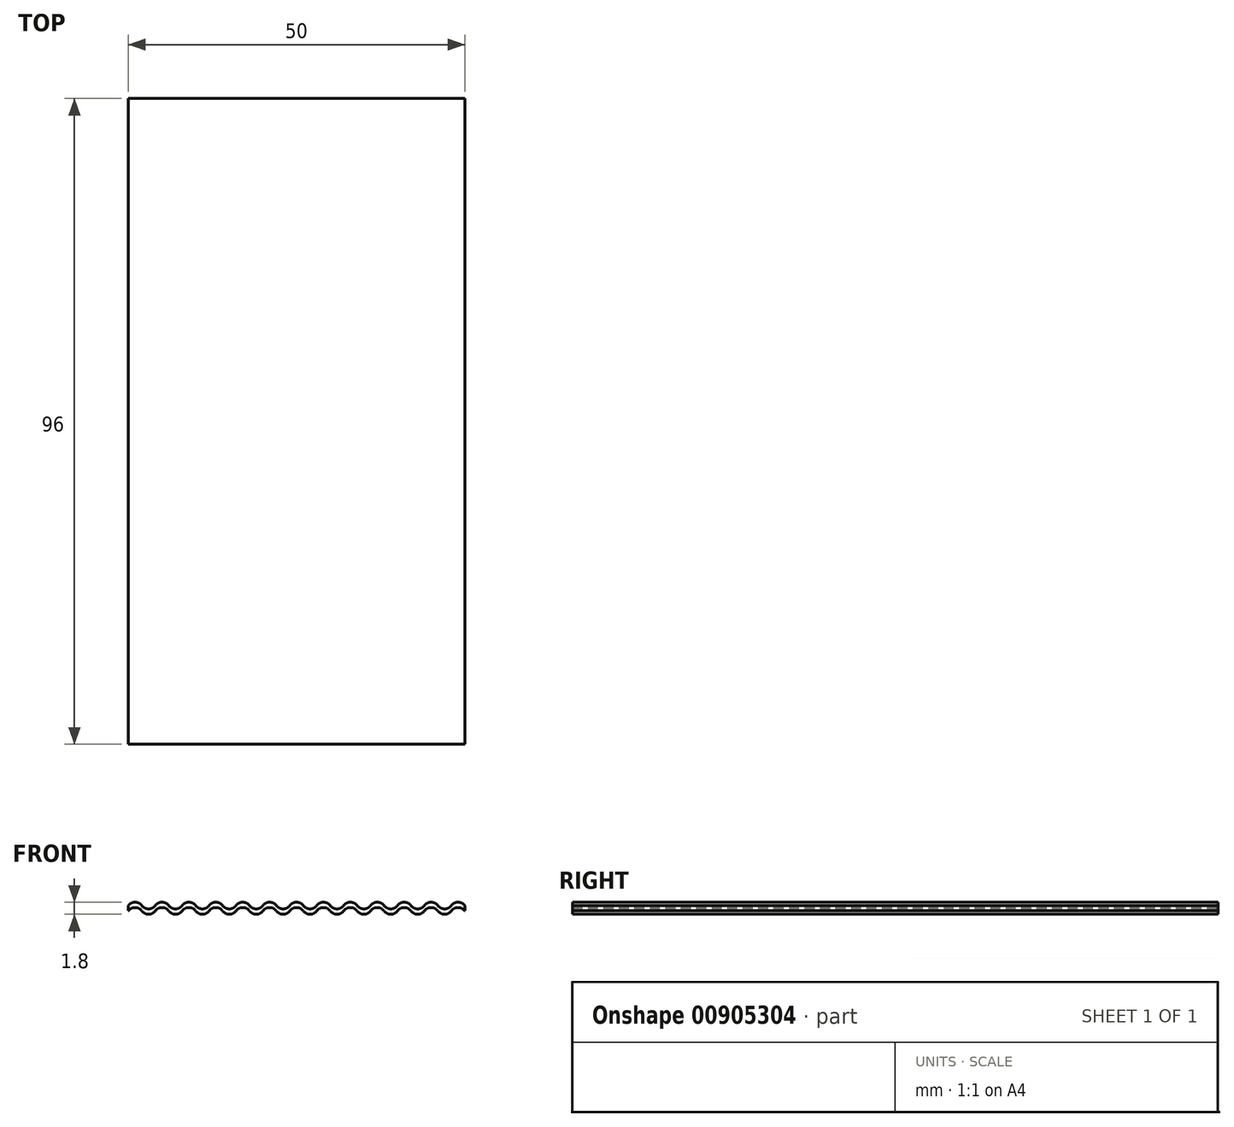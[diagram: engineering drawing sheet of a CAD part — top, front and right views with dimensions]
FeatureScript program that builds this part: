
annotation { "Feature Type Name" : "Feature", "Feature Type Description" : "" }
export const myFeature = defineFeature(function(context is Context, id is Id, definition is map)
    precondition{}
    {
        {
            var Q0;
            Q0=qCreatedBy(makeId("Front.planeOp"),FACE);
            var sketch = newSketch(context, id + "F0", { "sketchPlane" : qUnion([Q0])});
            skArc(sketch, "E0", {"start": v(-19, -0.4) * mm, "mid": v(-20, 0.1) * mm, "end": v(-21, -0.4) * mm});
            skArc(sketch, "E1", {"start": v(-23, -0.4) * mm, "mid": v(-22, -0.9) * mm, "end": v(-21, -0.4) * mm});
            skArc(sketch, "E2", {"start": v(-23, -0.4) * mm, "mid": v(-24, 0.1) * mm, "end": v(-25, -0.4) * mm});
            skArc(sketch, "E3", {"start": v(5, -0.4) * mm, "mid": v(6, -0.9) * mm, "end": v(7, -0.4) * mm});
            skArc(sketch, "E4", {"start": v(9, -0.4) * mm, "mid": v(8, 0.1) * mm, "end": v(7, -0.4) * mm});
            skArc(sketch, "E5", {"start": v(9, -0.4) * mm, "mid": v(10, -0.9) * mm, "end": v(11, -0.4) * mm});
            skArc(sketch, "E6", {"start": v(13, -0.4) * mm, "mid": v(12, 0.1) * mm, "end": v(11, -0.4) * mm});
            skArc(sketch, "E7", {"start": v(13, -0.4) * mm, "mid": v(14, -0.9) * mm, "end": v(15, -0.4) * mm});
            skArc(sketch, "E8", {"start": v(17, -0.4) * mm, "mid": v(16, 0.1) * mm, "end": v(15, -0.4) * mm});
            skArc(sketch, "E9", {"start": v(25, -0.4) * mm, "mid": v(24, 0.1) * mm, "end": v(23, -0.4) * mm});
            skArc(sketch, "E10", {"start": v(21, -0.4) * mm, "mid": v(22, -0.9) * mm, "end": v(23, -0.4) * mm});
            skArc(sketch, "E11", {"start": v(21, -0.4) * mm, "mid": v(20, 0.1) * mm, "end": v(19, -0.4) * mm});
            skArc(sketch, "E12", {"start": v(17, -0.4) * mm, "mid": v(18, -0.9) * mm, "end": v(19, -0.4) * mm});
            skArc(sketch, "E13", {"start": v(5, -0.4) * mm, "mid": v(4, 0.1) * mm, "end": v(3, -0.4) * mm});
            skArc(sketch, "E14", {"start": v(1, -0.4) * mm, "mid": v(2, -0.9) * mm, "end": v(3, -0.4) * mm});
            skArc(sketch, "E15", {"start": v(1, -0.4) * mm, "mid": v(0, 0.1) * mm, "end": v(-1, -0.4) * mm});
            skArc(sketch, "E16", {"start": v(-3, -0.4) * mm, "mid": v(-2, -0.9) * mm, "end": v(-1, -0.4) * mm});
            skArc(sketch, "E17", {"start": v(-3, -0.4) * mm, "mid": v(-4, 0.1) * mm, "end": v(-5, -0.4) * mm});
            skArc(sketch, "E18", {"start": v(-7, -0.4) * mm, "mid": v(-6, -0.9) * mm, "end": v(-5, -0.4) * mm});
            skArc(sketch, "E19", {"start": v(-7, -0.4) * mm, "mid": v(-8, 0.1) * mm, "end": v(-9, -0.4) * mm});
            skArc(sketch, "E20", {"start": v(-11, -0.4) * mm, "mid": v(-10, -0.9) * mm, "end": v(-9, -0.4) * mm});
            skArc(sketch, "E21", {"start": v(-11, -0.4) * mm, "mid": v(-12, 0.1) * mm, "end": v(-13, -0.4) * mm});
            skArc(sketch, "E22", {"start": v(-15, -0.4) * mm, "mid": v(-14, -0.9) * mm, "end": v(-13, -0.4) * mm});
            skArc(sketch, "E23", {"start": v(-15, -0.4) * mm, "mid": v(-16, 0.1) * mm, "end": v(-17, -0.4) * mm});
            skArc(sketch, "E24", {"start": v(-19, -0.4) * mm, "mid": v(-18, -0.9) * mm, "end": v(-17, -0.4) * mm});
            skArc(sketch, "E25", {"start": v(-19, 0.4) * mm, "mid": v(-20, 0.9) * mm, "end": v(-21, 0.4) * mm});
            skArc(sketch, "E26", {"start": v(-23, 0.4) * mm, "mid": v(-22, -0.1) * mm, "end": v(-21, 0.4) * mm});
            skArc(sketch, "E27", {"start": v(-23, 0.4) * mm, "mid": v(-24, 0.9) * mm, "end": v(-25, 0.4) * mm});
            skArc(sketch, "E28", {"start": v(5, 0.4) * mm, "mid": v(6, -0.1) * mm, "end": v(7, 0.4) * mm});
            skArc(sketch, "E29", {"start": v(9, 0.4) * mm, "mid": v(8, 0.9) * mm, "end": v(7, 0.4) * mm});
            skArc(sketch, "E30", {"start": v(9, 0.4) * mm, "mid": v(10, -0.1) * mm, "end": v(11, 0.4) * mm});
            skArc(sketch, "E31", {"start": v(13, 0.4) * mm, "mid": v(12, 0.9) * mm, "end": v(11, 0.4) * mm});
            skArc(sketch, "E32", {"start": v(13, 0.4) * mm, "mid": v(14, -0.1) * mm, "end": v(15, 0.4) * mm});
            skArc(sketch, "E33", {"start": v(17, 0.4) * mm, "mid": v(16, 0.9) * mm, "end": v(15, 0.4) * mm});
            skArc(sketch, "E34", {"start": v(25, 0.4) * mm, "mid": v(24, 0.9) * mm, "end": v(23, 0.4) * mm});
            skArc(sketch, "E35", {"start": v(21, 0.4) * mm, "mid": v(22, -0.1) * mm, "end": v(23, 0.4) * mm});
            skArc(sketch, "E36", {"start": v(21, 0.4) * mm, "mid": v(20, 0.9) * mm, "end": v(19, 0.4) * mm});
            skArc(sketch, "E37", {"start": v(17, 0.4) * mm, "mid": v(18, -0.1) * mm, "end": v(19, 0.4) * mm});
            skArc(sketch, "E38", {"start": v(5, 0.4) * mm, "mid": v(4, 0.9) * mm, "end": v(3, 0.4) * mm});
            skArc(sketch, "E39", {"start": v(1, 0.4) * mm, "mid": v(2, -0.1) * mm, "end": v(3, 0.4) * mm});
            skArc(sketch, "E40", {"start": v(1, 0.4) * mm, "mid": v(0, 0.9) * mm, "end": v(-1, 0.4) * mm});
            skArc(sketch, "E41", {"start": v(-3, 0.4) * mm, "mid": v(-2, -0.1) * mm, "end": v(-1, 0.4) * mm});
            skArc(sketch, "E42", {"start": v(-3, 0.4) * mm, "mid": v(-4, 0.9) * mm, "end": v(-5, 0.4) * mm});
            skArc(sketch, "E43", {"start": v(-7, 0.4) * mm, "mid": v(-6, -0.1) * mm, "end": v(-5, 0.4) * mm});
            skArc(sketch, "E44", {"start": v(-7, 0.4) * mm, "mid": v(-8, 0.9) * mm, "end": v(-9, 0.4) * mm});
            skArc(sketch, "E45", {"start": v(-11, 0.4) * mm, "mid": v(-10, -0.1) * mm, "end": v(-9, 0.4) * mm});
            skArc(sketch, "E46", {"start": v(-11, 0.4) * mm, "mid": v(-12, 0.9) * mm, "end": v(-13, 0.4) * mm});
            skArc(sketch, "E47", {"start": v(-15, 0.4) * mm, "mid": v(-14, -0.1) * mm, "end": v(-13, 0.4) * mm});
            skArc(sketch, "E48", {"start": v(-15, 0.4) * mm, "mid": v(-16, 0.9) * mm, "end": v(-17, 0.4) * mm});
            skArc(sketch, "E49", {"start": v(-19, 0.4) * mm, "mid": v(-18, -0.1) * mm, "end": v(-17, 0.4) * mm});
            skLineSegment(sketch, "E50", {"start": v(-25, 0.4) * mm, "end": v(-25, -0.4) * mm});
            skLineSegment(sketch, "E51", {"start": v(25, 0.4) * mm, "end": v(25, -0.4) * mm});
            skSolve(sketch);
        }
        {
            var Q0;
            Q0 = qSketchRegion(id + "F0", true);
            extrude(context, id + "F1", {"entities" : qUnion([Q0]), "depth" : 96 * mm, "offsetDistance" : 25 * mm});
        }
    });
